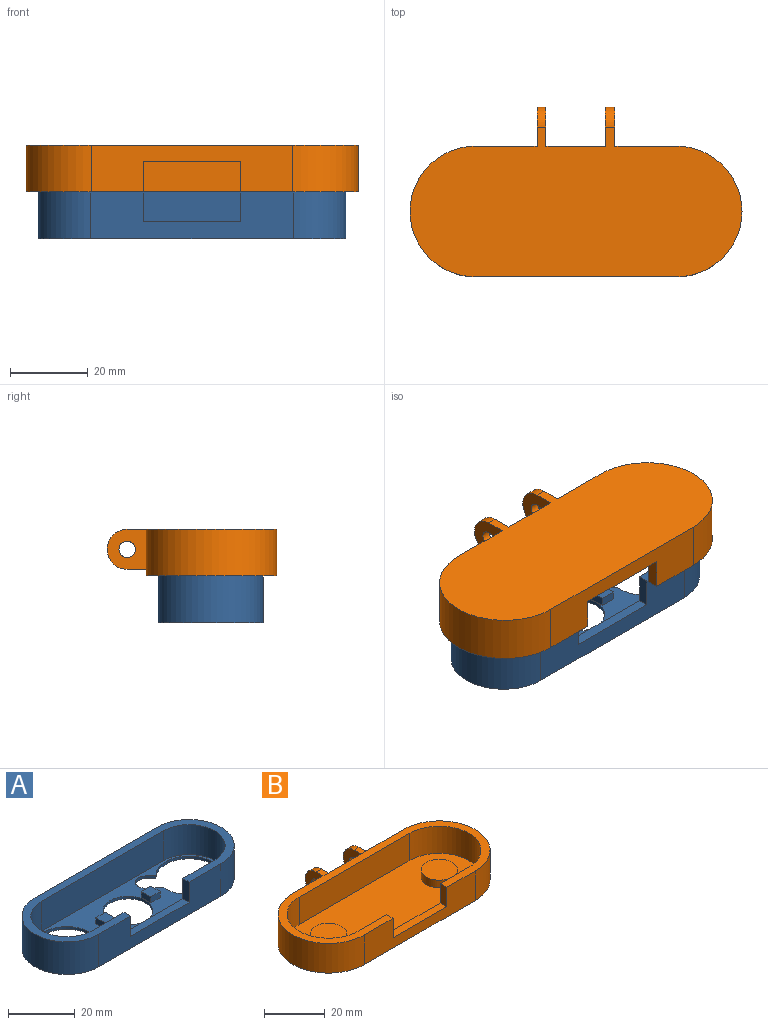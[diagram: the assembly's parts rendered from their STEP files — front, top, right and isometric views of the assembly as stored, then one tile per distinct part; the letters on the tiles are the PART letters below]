
ASSEMBLY  parts=2 mates=1
PART A: 33 faces, bbox 79x27x12 mm
  f0: plane 52x12mm, normal (0,-1,0), area 436.5mm2, adj f1,f7,f8,f9,f20,f21,f22
  f1: cylinder r=13.5mm len=27mm, axis (0,0,-1), area 508.9mm2, adj f0,f2,f8,f9
  f2: plane 52x12mm, normal (0,1,0), area 624mm2, adj f1,f7,f8,f9
  f3: plane 52x11mm, normal (0,1,0), area 384.5mm2, adj f4,f6,f8,f19,f20,f21,f22
  f4: cylinder r=10.8mm len=21.6mm, axis (0,0,-1), area 373.2mm2, adj f3,f5,f8,f19
  f5: plane 52x11mm, normal (0,-1,0), area 572mm2, adj f4,f6,f8,f19
  f6: cylinder r=10.8mm len=21.6mm, axis (0,0,-1), area 373.2mm2, adj f3,f5,f8,f19
  f7: cylinder r=13.5mm len=27mm, axis (0,0,-1), area 508.9mm2, adj f0,f2,f8,f9
  f8: plane 79x27mm, normal (0,0,1), area 419.4mm2, adj f0,f1,f2,f3,f4,f5,f6,f7
  f9: plane 79x27mm, normal (0,0,-1), area 1091.7mm2, adj f0,f1,f2,f7,f10,f11,f12,f13
  f10: plane 2.42x2.07mm, normal (-0.65,-0.76,0), area 3.2mm2, adj f9,f11,f16,f19
  f11: cylinder r=10mm len=20mm, axis (0,0,-1), area 55.9mm2, adj f9,f10,f12,f19
  f12: plane 3.74x3.19mm, normal (0.65,0.76,0), area 4.9mm2, adj f9,f11,f16,f19
  f13: plane 2.87x1.96mm, normal (0.56,0.83,0), area 3.5mm2, adj f9,f14,f17,f19
  f14: cylinder r=10mm len=20mm, axis (0,0,-1), area 56.5mm2, adj f9,f13,f15,f19
  f15: plane 3.31x1.88mm, normal (-0.49,-0.87,0), area 3.8mm2, adj f9,f14,f17,f19
  f16: cylinder r=3.25mm len=5.78mm, axis (0,0,-1), area 10.3mm2, adj f9,f10,f12,f19
  f17: cylinder r=3.25mm len=6.15mm, axis (0,0,-1), area 10.7mm2, adj f9,f13,f15,f19
  f18: cylinder r=7.5mm len=15mm, axis (0,0,-1), area 47.1mm2, adj f9,f19
  f19: plane 73.6x21.6mm, normal (0,0,1), area 572.8mm2, adj f3,f4,f5,f6,f10,f11,f12,f13
  f20: plane 25x2.7mm, normal (0,0,1), area 67.5mm2, adj f0,f3,f21,f22
  f21: plane 7.5x2.7mm, normal (-1,0,0), area 20.2mm2, adj f0,f3,f8,f20
  f22: plane 7.5x2.7mm, normal (1,0,0), area 20.2mm2, adj f0,f3,f8,f20
  f23: plane 4x2.2mm, normal (0,-1,0), area 8.8mm2, adj f19,f24,f26,f27
  f24: plane 4x2.2mm, normal (1,0,0), area 8.8mm2, adj f19,f23,f25,f27
  f25: plane 4x2.2mm, normal (0,1,0), area 8.8mm2, adj f19,f24,f26,f27
  f26: plane 4x2.2mm, normal (-1,0,0), area 8.8mm2, adj f19,f23,f25,f27
  f27: plane 4x4mm, normal (0,0,1), area 16mm2, adj f23,f24,f25,f26
  f28: plane 4x2.2mm, normal (0,1,0), area 8.8mm2, adj f19,f29,f31,f32
  f29: plane 4x2.2mm, normal (-1,0,0), area 8.8mm2, adj f19,f28,f30,f32
  f30: plane 4x2.2mm, normal (0,-1,0), area 8.8mm2, adj f19,f29,f31,f32
  f31: plane 4x2.2mm, normal (1,0,0), area 8.8mm2, adj f19,f28,f30,f32
  f32: plane 4x4mm, normal (0,0,1), area 16mm2, adj f28,f29,f30,f31
PART B: 29 faces, bbox 85.2x43.6x12 mm
  f0: cylinder r=5.14mm len=10.29mm, axis (-1,0,0), area 37.2mm2, adj f1,f12,f24,f28
  f1: plane 4.92x2.3mm, normal (0,0,1), area 11.3mm2, adj f0,f6,f24,f28
  f2: cylinder r=2.1mm len=4.2mm, axis (-1,0,0), area 30.3mm2, adj f24,f28
  f3: plane 51.7x12mm, normal (0,-1,0), area 425.4mm2, adj f5,f7,f11,f12,f14,f15,f16
  f4: plane 51.7x11mm, normal (0,1,0), area 373.7mm2, adj f5,f8,f10,f13,f14,f15,f16
  f5: plane 85.2x33.5mm, normal (0,0,1), area 522.7mm2, adj f3,f4,f6,f7,f8,f9,f10,f11
  f6: plane 51.7x12mm, normal (0,1,0), area 414.6mm2, adj f1,f5,f7,f11,f12,f22,f24,f25
  f7: cylinder r=16.75mm len=33.5mm, axis (0,0,-1), area 631.5mm2, adj f3,f5,f6,f12
  f8: cylinder r=13.75mm len=27.5mm, axis (0,0,-1), area 475.2mm2, adj f4,f5,f9,f13
  f9: plane 51.7x11mm, normal (0,-1,0), area 568.7mm2, adj f5,f8,f10,f13
  f10: cylinder r=13.75mm len=27.5mm, axis (0,0,-1), area 475.2mm2, adj f4,f5,f9,f13
  f11: cylinder r=16.75mm len=33.5mm, axis (0,0,-1), area 631.5mm2, adj f3,f5,f6,f12
  f12: plane 85.2x38.42mm, normal (0,0,-1), area 2637mm2, adj f0,f3,f6,f7,f11,f21,f24,f25
  f13: plane 79.2x27.5mm, normal (0,0,1), area 1789.5mm2, adj f4,f8,f9,f10,f18,f20
  f14: plane 25x3mm, normal (0,0,1), area 75mm2, adj f3,f4,f15,f16
  f15: plane 7.8x3mm, normal (-1,0,0), area 23.4mm2, adj f3,f4,f5,f14
  f16: plane 7.8x3mm, normal (1,0,0), area 23.4mm2, adj f3,f4,f5,f14
  f17: plane 12x12mm, normal (0,0,1), area 113.1mm2, adj f18
  f18: cylinder r=6mm len=12mm, axis (0,0,-1), area 116.9mm2, adj f13,f17
  f19: plane 12x12mm, normal (0,0,1), area 113.1mm2, adj f20
  f20: cylinder r=6mm len=12mm, axis (0,0,-1), area 116.9mm2, adj f13,f19
  f21: cylinder r=5.14mm len=10.29mm, axis (-1,0,0), area 40.4mm2, adj f12,f22,f25,f27
  f22: plane 4.92x2.5mm, normal (0,0,1), area 12.3mm2, adj f6,f21,f25,f27
  f23: cylinder r=2.1mm len=4.2mm, axis (-1,0,0), area 33mm2, adj f25,f27
  f24: plane 10.29x10.06mm, normal (1,0,0), area 78.3mm2, adj f0,f1,f2,f6,f12
  f25: plane 10.29x10.06mm, normal (-1,0,0), area 78.3mm2, adj f6,f12,f21,f22,f23
  f26: plane 15.2x10.29mm, normal (0,1,0), area 156.4mm2, adj f6,f12,f27,f28
  f27: plane 10.29x10.07mm, normal (1,0,0), area 78.3mm2, adj f12,f21,f22,f23,f26
  f28: plane 10.29x10.07mm, normal (-1,0,0), area 78.3mm2, adj f0,f1,f2,f12,f26
PLACE A t=(-25.3,-94.41,-14.77)mm
PLACE B rot(axis=(0,1,0),180deg) t=(-25.3,-96.39,9.23)mm
MATE fastened B.f5 <-> A.f8  axis (0,0,-1) through (-25.3,-92.46,-2.77)mm
